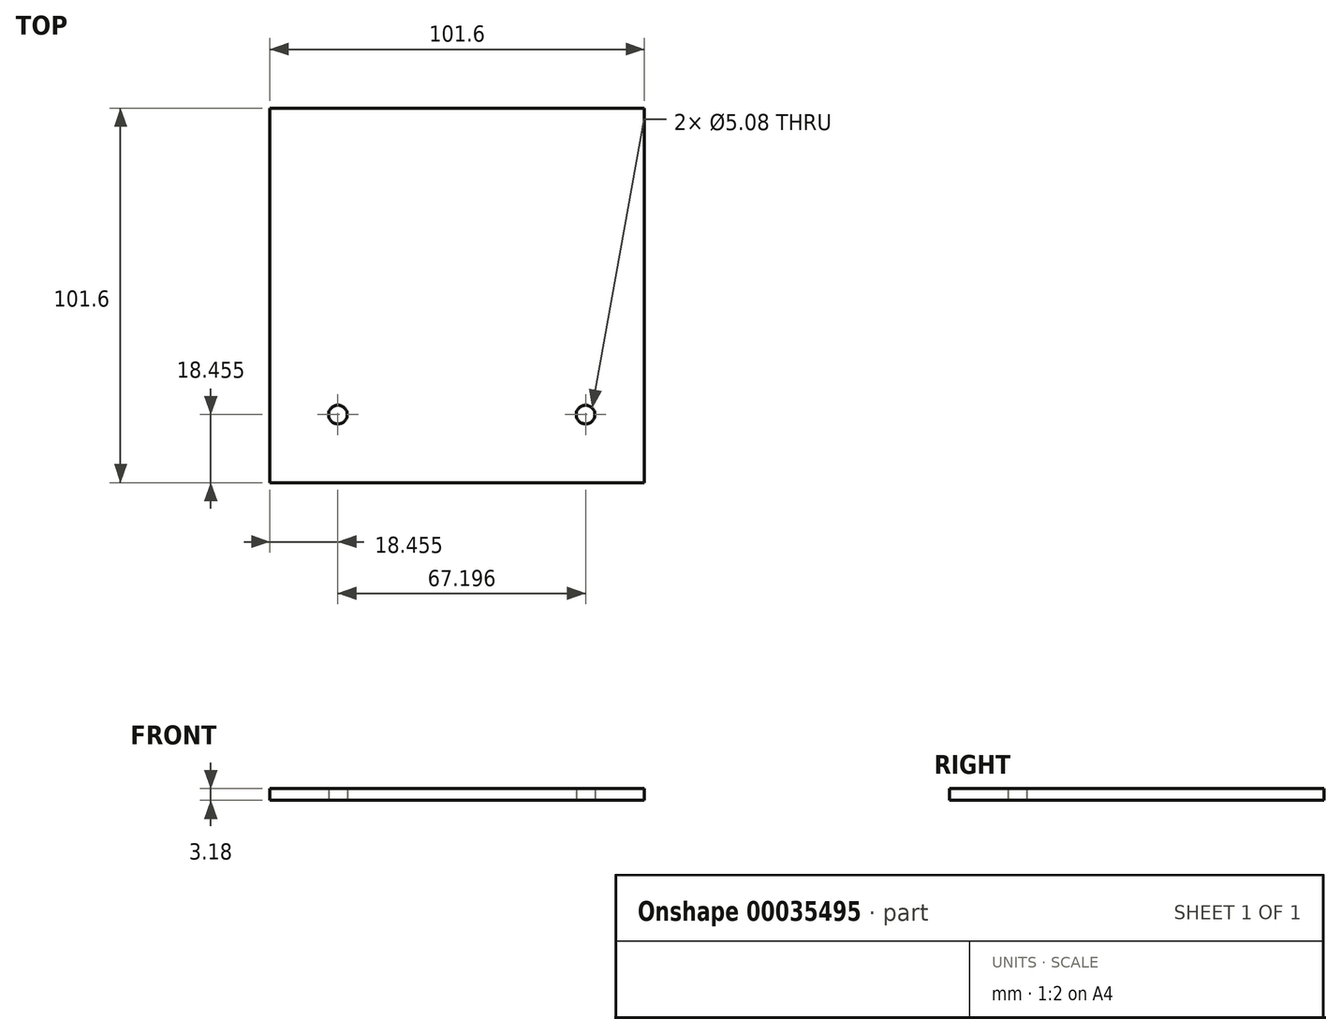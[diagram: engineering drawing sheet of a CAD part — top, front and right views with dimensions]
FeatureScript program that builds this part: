
annotation { "Feature Type Name" : "Feature", "Feature Type Description" : "" }
export const myFeature = defineFeature(function(context is Context, id is Id, definition is map)
    precondition{}
    {
        {
            var Q0;
            Q0=qCreatedBy(makeId("Top.planeOp"),FACE);
            var sketch = newSketch(context, id + "F0", { "sketchPlane" : qUnion([Q0])});
            skLineSegment(sketch, "E0.rect.bottom", {"start": v(50.8, 50.8) * mm, "end": v(-50.8, 50.8) * mm});
            skLineSegment(sketch, "E0.rect.top", {"start": v(50.8, -50.8) * mm, "end": v(-50.8, -50.8) * mm});
            skLineSegment(sketch, "E0.rect.left", {"start": v(50.8, 50.8) * mm, "end": v(50.8, -50.8) * mm});
            skLineSegment(sketch, "E0.rect.right", {"start": v(-50.8, 50.8) * mm, "end": v(-50.8, -50.8) * mm});
            skPoint(sketch, "E0.rect.middle", {"position": v(0, 0) * mm});
            skLineSegment(sketch, "E1", {"start": v(0, 0) * mm, "end": v(0, -82.41) * mm, "construction": true});
            skLineSegment(sketch, "E2", {"start": v(0, -82.41) * mm, "end": v(0, 70.45) * mm, "construction": true});
            skLineSegment(sketch, "E3", {"start": v(0, 70.45) * mm, "end": v(0, -32.34) * mm, "construction": true});
            skLineSegment(sketch, "E4", {"start": v(0, -32.34) * mm, "end": v(-64.69, -32.34) * mm, "construction": true});
            skLineSegment(sketch, "E5", {"start": v(-64.69, -32.34) * mm, "end": v(65.24, -32.34) * mm, "construction": true});
            skCircle(sketch, "E6", {"center": v(34.85, -32.34) * mm, "radius": 2.54 * mm});
            skCircle(sketch, "E7", {"center": v(-32.34, -32.34) * mm, "radius": 2.54 * mm});
            skSolve(sketch);
        }
        {
            var Q0;
            Q0=makeQuery(id+"F0.imprint","IMPRINT",FACE,{"disambiguationData":[TD([[makeQuery(id+"F0.imprint","IMPRINT",EDGE,{"derivedFrom":sQuery(id+"F0.wireOp",EDGE,"E0.rect.bottom")}),1.0]])]});
            extrude(context, id + "F1", {"entities" : qUnion([Q0]), "depth" : 3.17 * mm});
        }
    });
